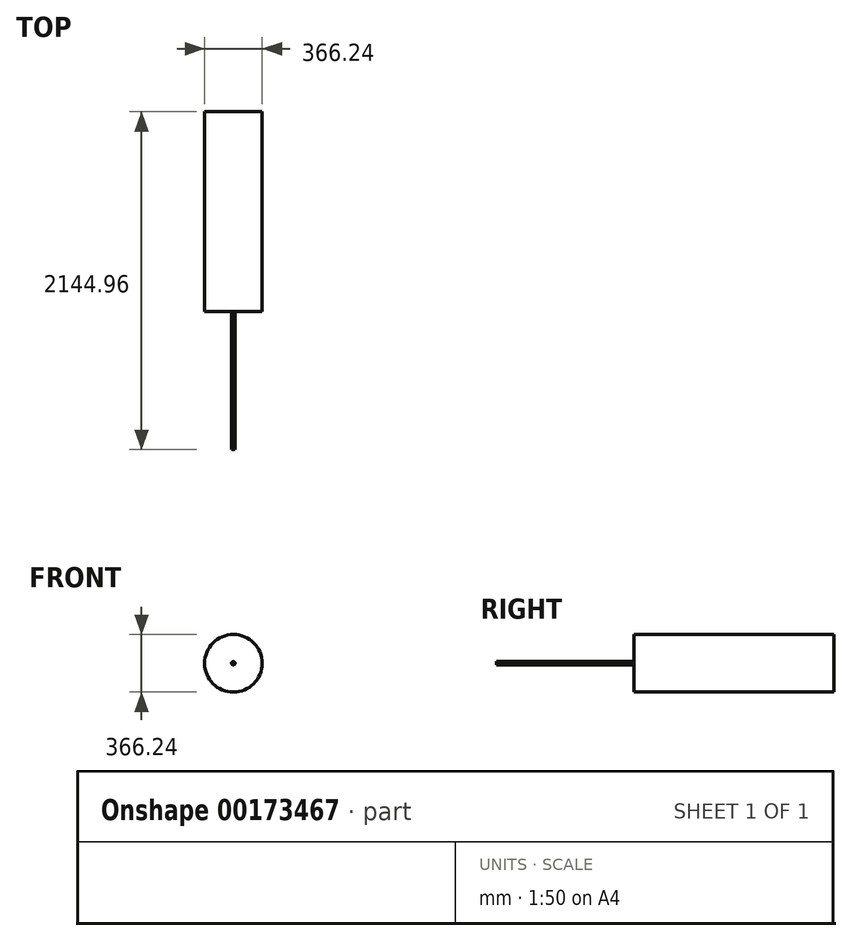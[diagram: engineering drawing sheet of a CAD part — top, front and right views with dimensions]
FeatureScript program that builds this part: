
annotation { "Feature Type Name" : "Feature", "Feature Type Description" : "" }
export const myFeature = defineFeature(function(context is Context, id is Id, definition is map)
    precondition{}
    {
        {
            var Q0;
            Q0=qCreatedBy(makeId("Front.planeOp"),FACE);
            var sketch = newSketch(context, id + "F4", { "sketchPlane" : qUnion([Q0])});
            skCircle(sketch, "E0", {"center": v(0, 0) * mm, "radius": 183.12 * mm});
            skSolve(sketch);
        }
        {
            var Q0;
            Q0=makeQuery(id+"F4.imprint","IMPRINT",FACE,{"disambiguationData":[TD([[makeQuery(id+"F4.imprint","IMPRINT",EDGE,{"derivedFrom":sQuery(id+"F4.wireOp",EDGE,"E0")}),1.0]])]});
            extrude(context, id + "F5", {"entities" : qUnion([Q0]), "oppositeDirection" : true, "depth" : 1270 * mm});
        }
        {
            var Q0;
            Q0=makeQuery(id+"F5.opExtrude","CAP_FACE",FACE,{"disambiguationData":[OSD([sQuery(id+"F4.wireOp",EDGE,"E0")])],"isStart":true});
            var sketch = newSketch(context, id + "F0", { "sketchPlane" : qUnion([Q0])});
            skCircle(sketch, "E1", {"center": v(-0.6, -0.06) * mm, "radius": 10.58 * mm});
            skSolve(sketch);
        }
        {
            var Q0;
            Q0=makeQuery(id+"F0.imprint","IMPRINT",FACE,{"disambiguationData":[TD([[makeQuery(id+"F0.imprint","IMPRINT",EDGE,{"derivedFrom":sQuery(id+"F0.wireOp",EDGE,"E1")}),1.0]])]});
            extrude(context, id + "F1", {"entities" : qUnion([Q0]), "operationType" : NewBodyOperationType.ADD, "depth" : 874.96 * mm, "hasSecondDirection" : true, "secondDirectionBound" : SecondDirectionBoundingType.UP_TO_NEXT, "secondDirectionOppositeDirection" : true, "secondDirectionDepth" : 25.4 * mm});
        }
    });
